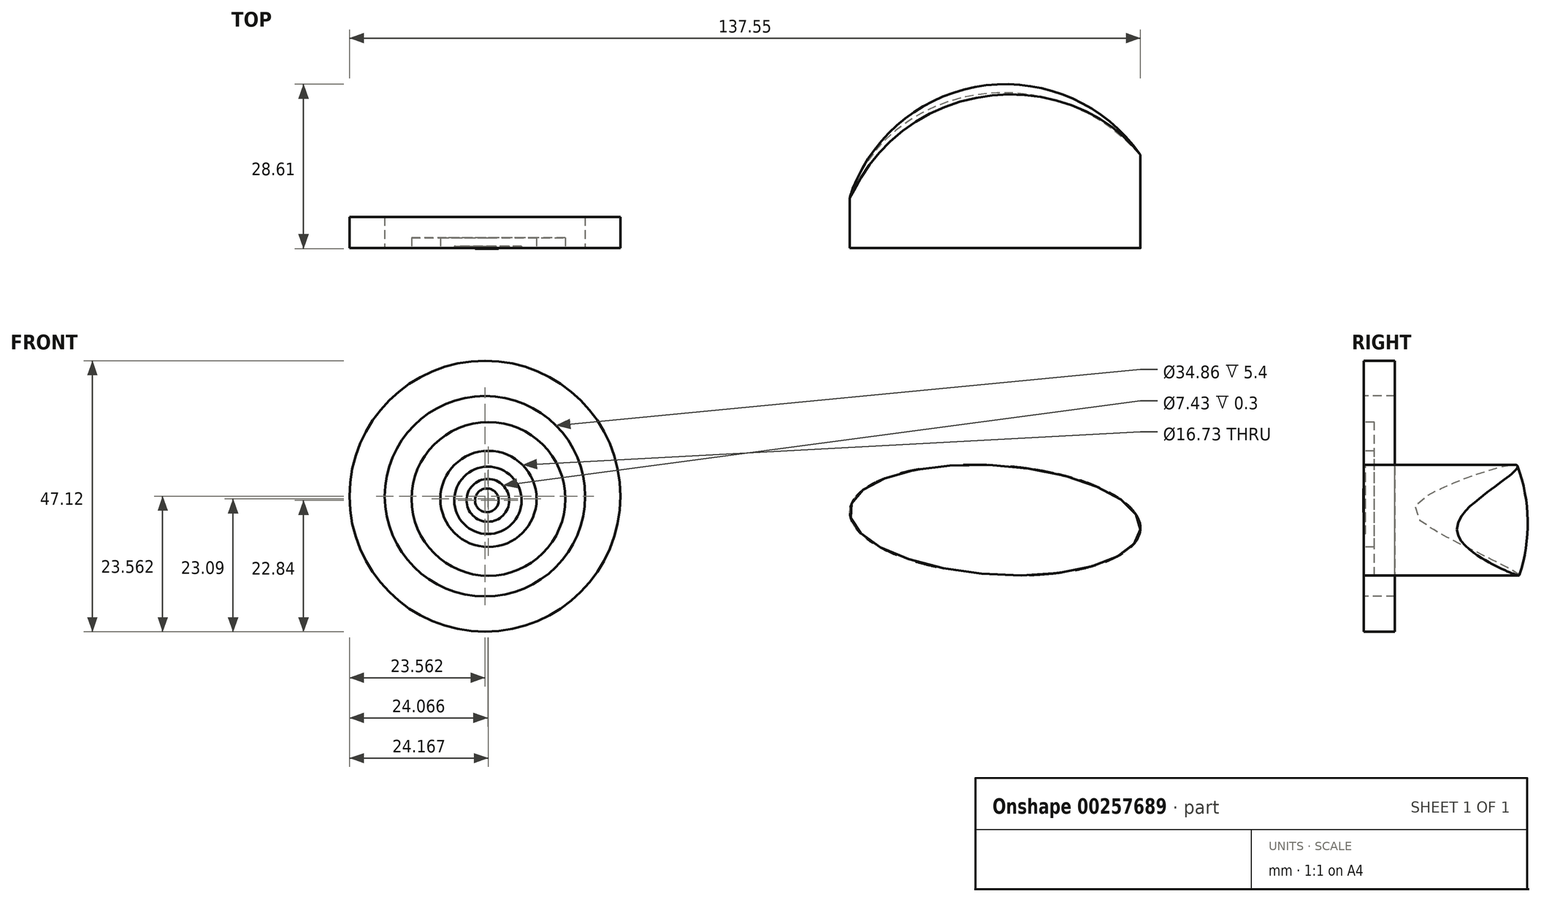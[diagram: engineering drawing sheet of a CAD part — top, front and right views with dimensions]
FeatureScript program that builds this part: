
annotation { "Feature Type Name" : "Feature", "Feature Type Description" : "" }
export const myFeature = defineFeature(function(context is Context, id is Id, definition is map)
    precondition{}
    {
        {
            var Q0;
            Q0=qCreatedBy(makeId("Top.planeOp"),FACE);
            var sketch = newSketch(context, id + "F0", { "sketchPlane" : qUnion([Q0])});
            skCircle(sketch, "E0", {"center": v(0, 0) * mm, "radius": 10 * mm});
            skSolve(sketch);
        }
        {
            var Q0;
            Q0=makeQuery(id+"F0.imprint","IMPRINT",FACE,{"disambiguationData":[TD([[makeQuery(id+"F0.imprint","IMPRINT",EDGE,{"derivedFrom":sQuery(id+"F0.wireOp",EDGE,"E0")}),1.0]])]});
            extrude(context, id + "F1", {"entities" : qUnion([Q0]), "depth" : 106 * mm, "hasDraft" : true, "draftAngle" : 16 * degree, "draftPullDirection" : true, "hasSecondDirection" : true, "secondDirectionOppositeDirection" : true, "secondDirectionDepth" : 45 * mm, "hasSecondDirectionDraft" : true, "secondDirectionDraftAngle" : 18 * degree});
        }
        {
            var Q0;
            Q0=qCreatedBy(makeId("Front.planeOp"),FACE);
            var sketch = newSketch(context, id + "F2", { "sketchPlane" : qUnion([Q0])});
            skArc(sketch, "E1", {"start": v(0, 60.34) * mm, "mid": v(-18.42, 42.61) * mm, "end": v(0, 24.89) * mm});
            skLineSegment(sketch, "E2", {"start": v(0, 60.34) * mm, "end": v(0, 24.89) * mm});
            skSolve(sketch);
        }
        {
            var Q0;
            Q0=makeQuery(id+"F2.imprint","IMPRINT",FACE,{"disambiguationData":[TD([[makeQuery(id+"F2.imprint","IMPRINT",EDGE,{"derivedFrom":sQuery(id+"F2.wireOp",EDGE,"E1")}),1.0]])]});
            var Q1;
            Q1=sQuery(id+"F2.wireOp",EDGE,"E2");
            revolve(context, id + "F3", {"operationType" : NewBodyOperationType.ADD, "entities" : qUnion([Q0]), "axis" : qUnion([Q1]), "revolveType" : RevolveType.FULL});
        }
        {
            var Q0;
            Q0=qCreatedBy(makeId("Front.planeOp"),FACE);
            var sketch = newSketch(context, id + "F4", { "sketchPlane" : qUnion([Q0])});
            skCircle(sketch, "E3", {"center": v(8.3, 48.26) * mm, "radius": 13.71 * mm});
            skSolve(sketch);
        }
        {
            var Q0;
            Q0=makeQuery(id+"F4.imprint","IMPRINT",FACE,{"disambiguationData":[TD([[makeQuery(id+"F4.imprint","IMPRINT",EDGE,{"derivedFrom":sQuery(id+"F4.wireOp",EDGE,"E3")}),1.0]])]});
            extrude(context, id + "F5", {"entities" : qUnion([Q0]), "operationType" : NewBodyOperationType.REMOVE, "oppositeDirection" : true, "depth" : 25 * mm, "hasSecondDirection" : true, "secondDirectionOppositeDirection" : false, "secondDirectionDepth" : 31.1 * mm});
        }
        {
            var Q0;
            Q0=qCreatedBy(makeId("Front.planeOp"),FACE);
            var sketch = newSketch(context, id + "F6", { "sketchPlane" : qUnion([Q0])});
            skLineSegment(sketch, "E4", {"start": v(44.74, 55.12) * mm, "end": v(44.74, 26.61) * mm});
            skArc(sketch, "E5", {"start": v(44.74, 55.12) * mm, "mid": v(16.24, 26.61) * mm, "end": v(44.74, -1.9) * mm});
            skLineSegment(sketch, "E6", {"start": v(44.74, 26.61) * mm, "end": v(44.74, -1.9) * mm});
            skSolve(sketch);
        }
        {
            var Q0;
            Q0=makeQuery(id+"F6.imprint","IMPRINT",FACE,{"disambiguationData":[TD([[makeQuery(id+"F6.imprint","IMPRINT",EDGE,{"derivedFrom":sQuery(id+"F6.wireOp",EDGE,"E4")}),-1.0]])]});
            var Q1;
            Q1=sQuery(id+"F6.wireOp",EDGE,"E6");
            revolve(context, id + "F7", {"entities" : qUnion([Q0]), "axis" : qUnion([Q1]), "revolveType" : RevolveType.FULL});
        }
        {
            var Q0;
            Q0=qCreatedBy(makeId("Front.planeOp"),FACE);
            var sketch = newSketch(context, id + "F8", { "sketchPlane" : qUnion([Q0])});
            skEllipse(sketch, "E7", {"center": v(42.94, 27.15) * mm, "majorRadius": 25.3 * mm, "minorRadius": 9.5 * mm, "majorAxis": v(1, -0.06)});
            skSolve(sketch);
        }
        {
            var Q0;
            Q0 = qSketchRegion(id + "F8", true);
            extrude(context, id + "F9", {"entities" : qUnion([Q0]), "operationType" : NewBodyOperationType.INTERSECT, "oppositeDirection" : true, "depth" : 89.7 * mm});
        }
        {
            var Q0;
            Q0=qCreatedBy(makeId("Front.planeOp"),FACE);
            var sketch = newSketch(context, id + "F10", { "sketchPlane" : qUnion([Q0])});
            skCircle(sketch, "E8", {"center": v(-45.79, 31.3) * mm, "radius": 23.56 * mm});
            skCircle(sketch, "E9", {"center": v(-45.79, 31.3) * mm, "radius": 8.93 * mm});
            skCircle(sketch, "E10", {"center": v(-45.79, 31.3) * mm, "radius": 3.65 * mm});
            skCircle(sketch, "E11", {"center": v(-45.79, 31.3) * mm, "radius": 17.43 * mm});
            skSolve(sketch);
        }
        {
            var Q0;
            Q0 = qSketchRegion(id + "F10", true);
            extrude(context, id + "F11", {"entities" : qUnion([Q0]), "oppositeDirection" : true, "depth" : 5.4 * mm});
        }
        {
            var Q0;
            Q0=qCreatedBy(makeId("Front.planeOp"),FACE);
            var sketch = newSketch(context, id + "F12", { "sketchPlane" : qUnion([Q0])});
            skCircle(sketch, "E12", {"center": v(-45.18, 30.83) * mm, "radius": 13.37 * mm});
            skCircle(sketch, "E13", {"center": v(-45.18, 30.83) * mm, "radius": 8.37 * mm});
            skSolve(sketch);
        }
        {
            var Q0;
            Q0 = qSketchRegion(id + "F12", true);
            extrude(context, id + "F13", {"entities" : qUnion([Q0]), "oppositeDirection" : true, "depth" : 1.8 * mm});
        }
        {
            var Q0;
            Q0=qCreatedBy(makeId("Front.planeOp"),FACE);
            var sketch = newSketch(context, id + "F14", { "sketchPlane" : qUnion([Q0])});
            skCircle(sketch, "E14", {"center": v(-45.28, 30.58) * mm, "radius": 5.85 * mm});
            skCircle(sketch, "E15", {"center": v(-45.28, 30.58) * mm, "radius": 3.71 * mm});
            skSolve(sketch);
        }
        {
            var Q0;
            Q0 = qSketchRegion(id + "F14", true);
            extrude(context, id + "F15", {"entities" : qUnion([Q0]), "oppositeDirection" : true, "depth" : 0.3 * mm});
        }
        {
            var Q0;
            Q0=qCreatedBy(makeId("Front.planeOp"),FACE);
            var sketch = newSketch(context, id + "F16", { "sketchPlane" : qUnion([Q0])});
            skCircle(sketch, "E16", {"center": v(-45.46, 30.58) * mm, "radius": 2.06 * mm});
            skSolve(sketch);
        }
        {
            var Q0;
            Q0 = qSketchRegion(id + "F16", true);
            extrude(context, id + "F17", {"entities" : qUnion([Q0]), "depth" : 0.1 * mm});
        }
    });
